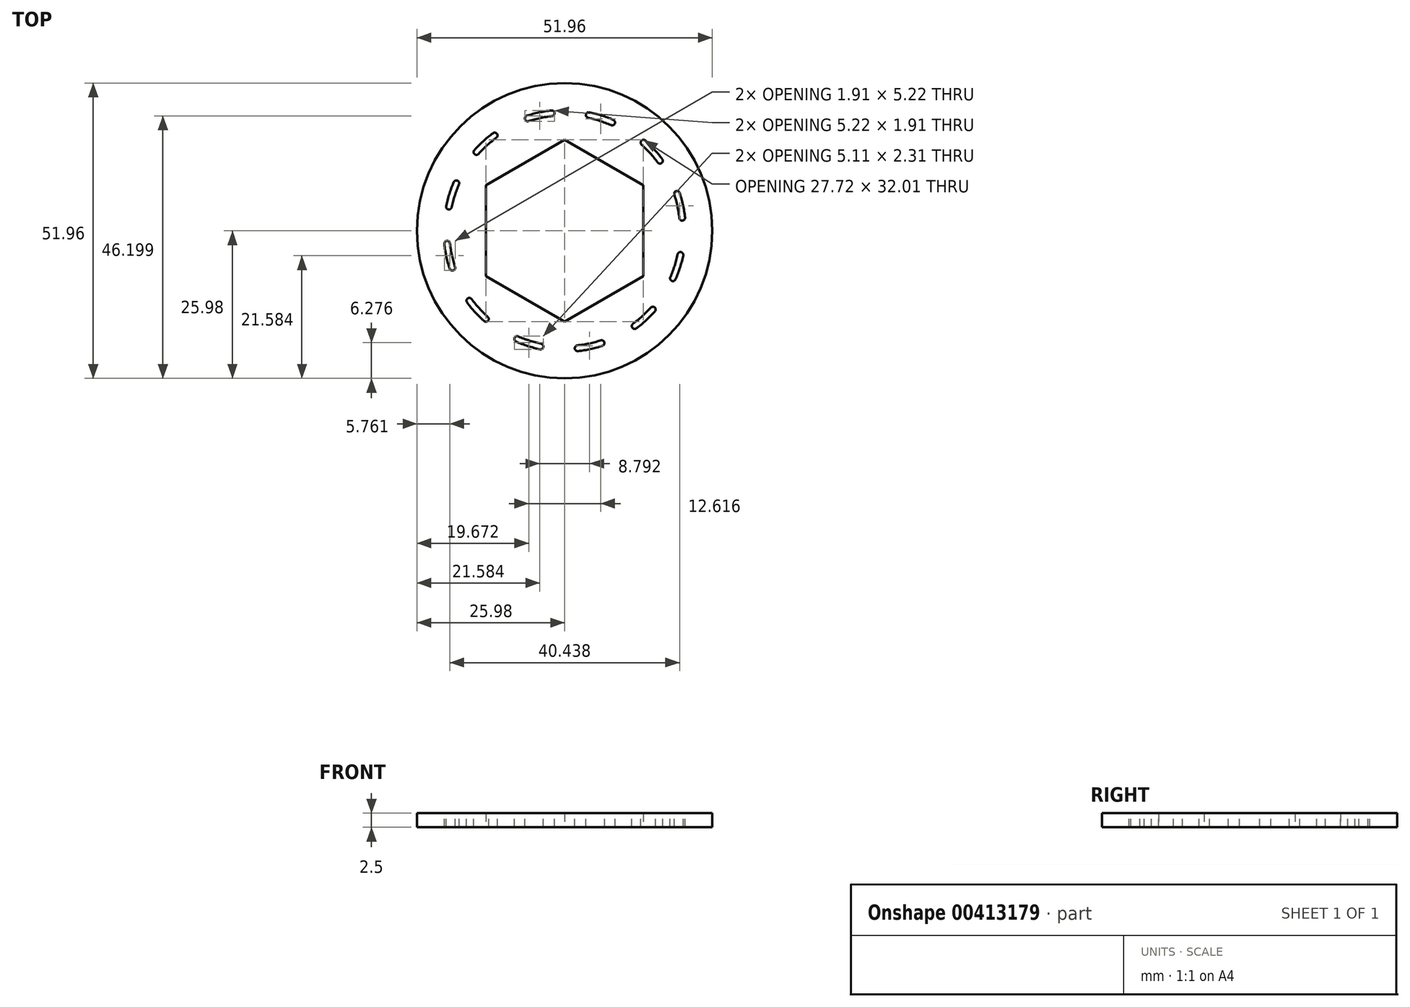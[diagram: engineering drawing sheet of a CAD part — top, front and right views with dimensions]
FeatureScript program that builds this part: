
annotation { "Feature Type Name" : "Feature", "Feature Type Description" : "" }
export const myFeature = defineFeature(function(context is Context, id is Id, definition is map)
    precondition{}
    {
        {
            var Q0;
            Q0=qCreatedBy(makeId("Top.planeOp"),FACE);
            var sketch = newSketch(context, id + "F0", { "sketchPlane" : qUnion([Q0])});
            skCircle(sketch, "E0", {"center": v(0, 0) * mm, "radius": 25.98 * mm});
            skCircle(sketch, "E1.cCircle", {"center": v(0, 0) * mm, "radius": 16 * mm, "construction": true});
            skLineSegment(sketch, "E1.0", {"start": v(0, 16) * mm, "end": v(13.86, 8) * mm});
            skLineSegment(sketch, "E1.1", {"start": v(13.86, 8) * mm, "end": v(13.86, -8) * mm});
            skLineSegment(sketch, "E1.2", {"start": v(13.86, -8) * mm, "end": v(0, -16) * mm});
            skLineSegment(sketch, "E1.3", {"start": v(0, -16) * mm, "end": v(-13.86, -8) * mm});
            skLineSegment(sketch, "E1.4", {"start": v(-13.86, -8) * mm, "end": v(-13.86, 8) * mm});
            skLineSegment(sketch, "E1.5", {"start": v(-13.86, 8) * mm, "end": v(0, 16) * mm});
            skSolve(sketch);
        }
        {
            var Q0;
            Q0 = qSketchRegion(id + "F0", true);
            extrude(context, id + "F1", {"entities" : qUnion([Q0]), "depth" : 2.5 * mm});
        }
        {
            var Q0;
            Q0=makeQuery(id+"F1.opExtrude","CAP_FACE",FACE,{"disambiguationData":[OSD([sQuery(id+"F0.wireOp",EDGE,"E0"),sQuery(id+"F0.wireOp",EDGE,"E1.0"),sQuery(id+"F0.wireOp",EDGE,"E1.1"),sQuery(id+"F0.wireOp",EDGE,"E1.2"),sQuery(id+"F0.wireOp",EDGE,"E1.3"),sQuery(id+"F0.wireOp",EDGE,"E1.4"),sQuery(id+"F0.wireOp",EDGE,"E1.5")])],"isStart":false});
            var sketch = newSketch(context, id + "F2", { "sketchPlane" : qUnion([Q0])});
            skArc(sketch, "E2", {"start": v(16.77, 12.32) * mm, "mid": v(15.4, 14) * mm, "end": v(13.86, 15.52) * mm});
            skArc(sketch, "E3.0.startCap", {"start": v(17.17, 12.61) * mm, "mid": v(17.06, 11.91) * mm, "end": v(16.36, 12.02) * mm});
            skArc(sketch, "E3.0.endCap", {"start": v(13.53, 15.14) * mm, "mid": v(13.49, 15.85) * mm, "end": v(14.2, 15.89) * mm});
            skArc(sketch, "E3.0.left", {"start": v(16.36, 12.02) * mm, "mid": v(15.03, 13.66) * mm, "end": v(13.53, 15.14) * mm});
            skArc(sketch, "E3.0.right", {"start": v(17.17, 12.61) * mm, "mid": v(15.77, 14.33) * mm, "end": v(14.2, 15.89) * mm});
            skArc(sketch, "E4.1.0", {"start": v(8.56, 19.5) * mm, "mid": v(6.5, 20.3) * mm, "end": v(4.35, 20.86) * mm});
            skArc(sketch, "E4.1.1", {"start": v(8.16, 18.6) * mm, "mid": v(6.19, 19.34) * mm, "end": v(4.14, 19.88) * mm});
            skArc(sketch, "E4.1.2", {"start": v(4.14, 19.88) * mm, "mid": v(3.76, 20.47) * mm, "end": v(4.35, 20.86) * mm});
            skArc(sketch, "E4.1.3", {"start": v(8.56, 19.5) * mm, "mid": v(8.82, 18.85) * mm, "end": v(8.16, 18.6) * mm});
            skArc(sketch, "E4.2.0", {"start": v(-2.34, 21.18) * mm, "mid": v(-4.53, 20.82) * mm, "end": v(-6.66, 20.24) * mm});
            skArc(sketch, "E4.2.1", {"start": v(-2.23, 20.18) * mm, "mid": v(-4.31, 19.84) * mm, "end": v(-6.35, 19.29) * mm});
            skArc(sketch, "E4.2.2", {"start": v(-6.35, 19.29) * mm, "mid": v(-6.98, 19.6) * mm, "end": v(-6.66, 20.24) * mm});
            skArc(sketch, "E4.2.3", {"start": v(-2.34, 21.18) * mm, "mid": v(-1.79, 20.73) * mm, "end": v(-2.23, 20.18) * mm});
            skArc(sketch, "E4.3.0", {"start": v(-12.61, 17.17) * mm, "mid": v(-14.33, 15.77) * mm, "end": v(-15.89, 14.2) * mm});
            skArc(sketch, "E4.3.1", {"start": v(-12.02, 16.36) * mm, "mid": v(-13.66, 15.03) * mm, "end": v(-15.14, 13.53) * mm});
            skArc(sketch, "E4.3.2", {"start": v(-15.14, 13.53) * mm, "mid": v(-15.85, 13.49) * mm, "end": v(-15.89, 14.2) * mm});
            skArc(sketch, "E4.3.3", {"start": v(-12.61, 17.17) * mm, "mid": v(-11.91, 17.06) * mm, "end": v(-12.02, 16.36) * mm});
            skArc(sketch, "E4.4.0", {"start": v(-19.5, 8.56) * mm, "mid": v(-20.3, 6.5) * mm, "end": v(-20.86, 4.35) * mm});
            skArc(sketch, "E4.4.1", {"start": v(-18.6, 8.16) * mm, "mid": v(-19.34, 6.19) * mm, "end": v(-19.88, 4.14) * mm});
            skArc(sketch, "E4.4.2", {"start": v(-19.88, 4.14) * mm, "mid": v(-20.47, 3.76) * mm, "end": v(-20.86, 4.35) * mm});
            skArc(sketch, "E4.4.3", {"start": v(-19.5, 8.56) * mm, "mid": v(-18.85, 8.82) * mm, "end": v(-18.6, 8.16) * mm});
            skArc(sketch, "E4.5.0", {"start": v(-21.18, -2.34) * mm, "mid": v(-20.82, -4.53) * mm, "end": v(-20.24, -6.66) * mm});
            skArc(sketch, "E4.5.1", {"start": v(-20.18, -2.23) * mm, "mid": v(-19.84, -4.31) * mm, "end": v(-19.29, -6.35) * mm});
            skArc(sketch, "E4.5.2", {"start": v(-19.29, -6.35) * mm, "mid": v(-19.6, -6.98) * mm, "end": v(-20.24, -6.66) * mm});
            skArc(sketch, "E4.5.3", {"start": v(-21.18, -2.34) * mm, "mid": v(-20.73, -1.79) * mm, "end": v(-20.18, -2.23) * mm});
            skArc(sketch, "E4.6.0", {"start": v(-17.17, -12.61) * mm, "mid": v(-15.77, -14.33) * mm, "end": v(-14.2, -15.89) * mm});
            skArc(sketch, "E4.6.1", {"start": v(-16.36, -12.02) * mm, "mid": v(-15.03, -13.66) * mm, "end": v(-13.53, -15.14) * mm});
            skArc(sketch, "E4.6.2", {"start": v(-13.53, -15.14) * mm, "mid": v(-13.49, -15.85) * mm, "end": v(-14.2, -15.89) * mm});
            skArc(sketch, "E4.6.3", {"start": v(-17.17, -12.61) * mm, "mid": v(-17.06, -11.91) * mm, "end": v(-16.36, -12.02) * mm});
            skArc(sketch, "E4.7.0", {"start": v(-8.56, -19.5) * mm, "mid": v(-6.5, -20.3) * mm, "end": v(-4.35, -20.86) * mm});
            skArc(sketch, "E4.7.1", {"start": v(-8.16, -18.6) * mm, "mid": v(-6.19, -19.34) * mm, "end": v(-4.14, -19.88) * mm});
            skArc(sketch, "E4.7.2", {"start": v(-4.14, -19.88) * mm, "mid": v(-3.76, -20.47) * mm, "end": v(-4.35, -20.86) * mm});
            skArc(sketch, "E4.7.3", {"start": v(-8.56, -19.5) * mm, "mid": v(-8.82, -18.85) * mm, "end": v(-8.16, -18.6) * mm});
            skArc(sketch, "E4.8.0", {"start": v(2.34, -21.18) * mm, "mid": v(4.53, -20.82) * mm, "end": v(6.66, -20.24) * mm});
            skArc(sketch, "E4.8.1", {"start": v(2.23, -20.18) * mm, "mid": v(4.31, -19.84) * mm, "end": v(6.35, -19.29) * mm});
            skArc(sketch, "E4.8.2", {"start": v(6.35, -19.29) * mm, "mid": v(6.98, -19.6) * mm, "end": v(6.66, -20.24) * mm});
            skArc(sketch, "E4.8.3", {"start": v(2.34, -21.18) * mm, "mid": v(1.79, -20.73) * mm, "end": v(2.23, -20.18) * mm});
            skArc(sketch, "E4.9.0", {"start": v(12.61, -17.17) * mm, "mid": v(14.33, -15.77) * mm, "end": v(15.89, -14.2) * mm});
            skArc(sketch, "E4.9.1", {"start": v(12.02, -16.36) * mm, "mid": v(13.66, -15.03) * mm, "end": v(15.14, -13.53) * mm});
            skArc(sketch, "E4.9.2", {"start": v(15.14, -13.53) * mm, "mid": v(15.85, -13.49) * mm, "end": v(15.89, -14.2) * mm});
            skArc(sketch, "E4.9.3", {"start": v(12.61, -17.17) * mm, "mid": v(11.91, -17.06) * mm, "end": v(12.02, -16.36) * mm});
            skArc(sketch, "E4.10.0", {"start": v(19.5, -8.56) * mm, "mid": v(20.3, -6.5) * mm, "end": v(20.86, -4.35) * mm});
            skArc(sketch, "E4.10.1", {"start": v(18.6, -8.16) * mm, "mid": v(19.34, -6.19) * mm, "end": v(19.88, -4.14) * mm});
            skArc(sketch, "E4.10.2", {"start": v(19.88, -4.14) * mm, "mid": v(20.47, -3.76) * mm, "end": v(20.86, -4.35) * mm});
            skArc(sketch, "E4.10.3", {"start": v(19.5, -8.56) * mm, "mid": v(18.85, -8.82) * mm, "end": v(18.6, -8.16) * mm});
            skArc(sketch, "E4.11.0", {"start": v(21.18, 2.34) * mm, "mid": v(20.82, 4.53) * mm, "end": v(20.24, 6.66) * mm});
            skArc(sketch, "E4.11.1", {"start": v(20.18, 2.23) * mm, "mid": v(19.84, 4.31) * mm, "end": v(19.29, 6.35) * mm});
            skArc(sketch, "E4.11.2", {"start": v(19.29, 6.35) * mm, "mid": v(19.6, 6.98) * mm, "end": v(20.24, 6.66) * mm});
            skArc(sketch, "E4.11.3", {"start": v(21.18, 2.34) * mm, "mid": v(20.73, 1.79) * mm, "end": v(20.18, 2.23) * mm});
            skSolve(sketch);
        }
        {
            var Q0;
            Q0 = qSketchRegion(id + "F2", true);
            extrude(context, id + "F3", {"entities" : qUnion([Q0]), "operationType" : NewBodyOperationType.REMOVE, "oppositeDirection" : true, "depth" : 3 * mm});
        }
    });
